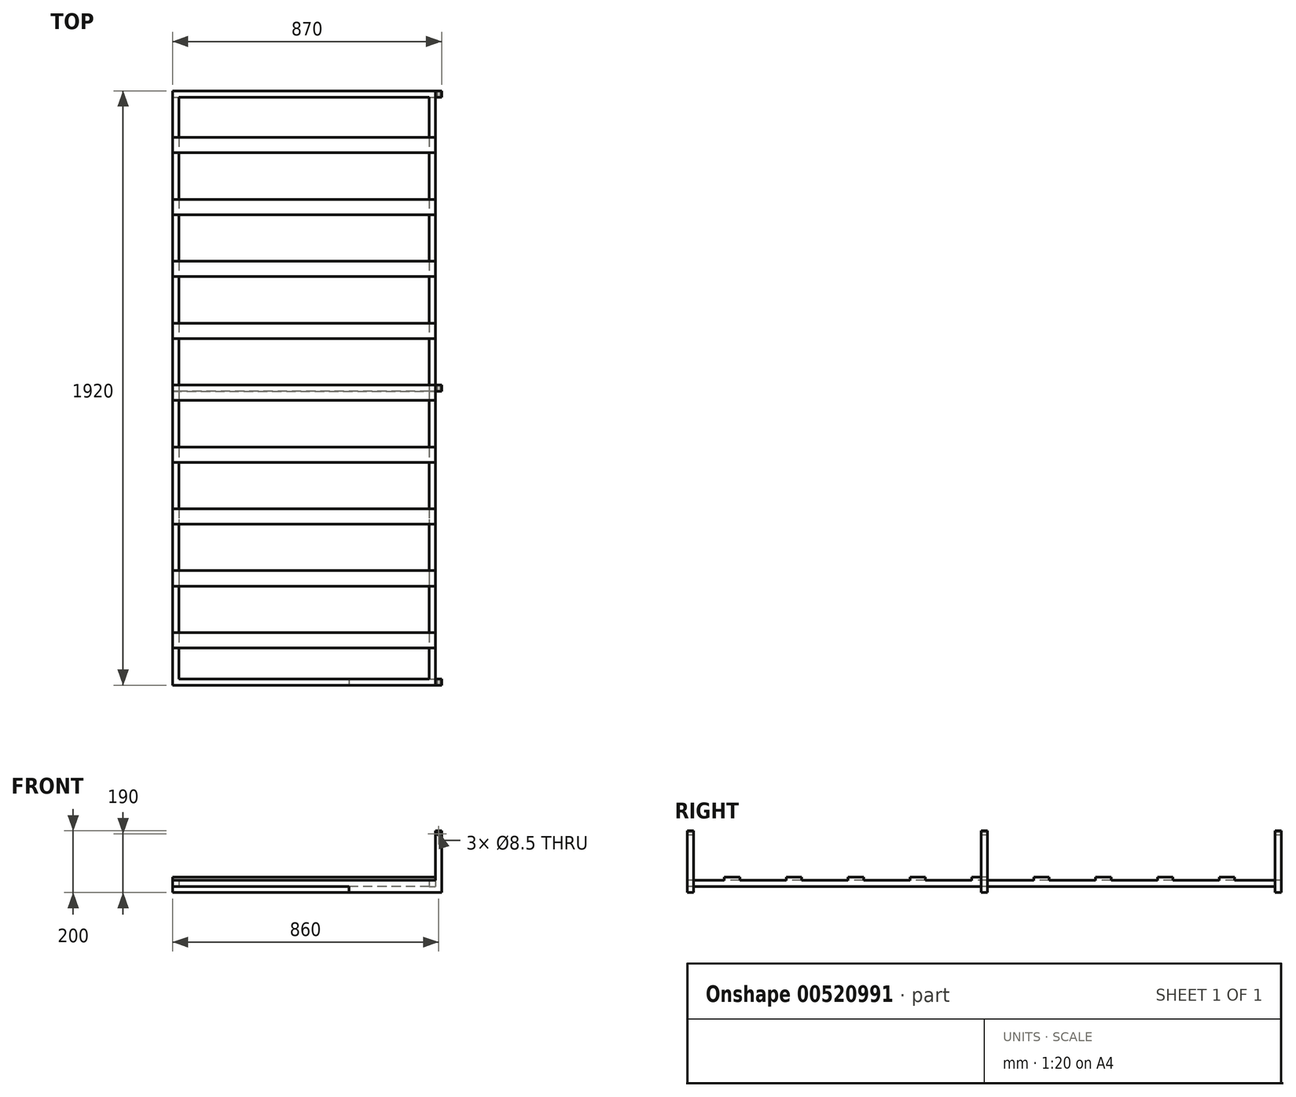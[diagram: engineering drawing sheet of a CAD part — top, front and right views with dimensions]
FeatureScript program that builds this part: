
annotation { "Feature Type Name" : "Feature", "Feature Type Description" : "" }
export const myFeature = defineFeature(function(context is Context, id is Id, definition is map)
    precondition{}
    {
        {
            var Q0;
            Q0=qCreatedBy(makeId("Top.planeOp"),FACE);
            var sketch = newSketch(context, id + "F0", { "sketchPlane" : qUnion([Q0])});
            skLineSegment(sketch, "E0.bottom", {"start": v(-425, 960) * mm, "end": v(425, 960) * mm});
            skLineSegment(sketch, "E0.top", {"start": v(-425, -960) * mm, "end": v(425, -960) * mm});
            skLineSegment(sketch, "E0.left", {"start": v(-425, 960) * mm, "end": v(-425, -960) * mm});
            skLineSegment(sketch, "E0.right", {"start": v(425, 960) * mm, "end": v(425, -960) * mm});
            skPoint(sketch, "E0.middle", {"position": v(0, 0) * mm});
            skLineSegment(sketch, "E1.0", {"start": v(405, 940) * mm, "end": v(405, -940) * mm});
            skLineSegment(sketch, "E1.1", {"start": v(-405, 940) * mm, "end": v(405, 940) * mm});
            skLineSegment(sketch, "E1.2", {"start": v(-405, 940) * mm, "end": v(-405, -940) * mm});
            skLineSegment(sketch, "E1.3", {"start": v(-405, -940) * mm, "end": v(405, -940) * mm});
            skSolve(sketch);
        }
        {
            var Q0;
            Q0 = qSketchRegion(id + "F0", true);
            extrude(context, id + "F1", {"entities" : qUnion([Q0]), "depth" : 20 * mm, "offsetDistance" : 25 * mm});
        }
        {
            var Q0;
            Q0=makeQuery(id+"F1.opExtrude","CAP_FACE",FACE,{"disambiguationData":[OSD([sQuery(id+"F0.wireOp",EDGE,"E0.bottom"),sQuery(id+"F0.wireOp",EDGE,"E0.top"),sQuery(id+"F0.wireOp",EDGE,"E0.left"),sQuery(id+"F0.wireOp",EDGE,"E0.right"),sQuery(id+"F0.wireOp",EDGE,"E1.0"),sQuery(id+"F0.wireOp",EDGE,"E1.1"),sQuery(id+"F0.wireOp",EDGE,"E1.2"),sQuery(id+"F0.wireOp",EDGE,"E1.3")])],"isStart":false});
            var sketch = newSketch(context, id + "F2", { "sketchPlane" : qUnion([Q0])});
            skLineSegment(sketch, "E2.bottom", {"start": v(-425, 810) * mm, "end": v(425, 810) * mm});
            skLineSegment(sketch, "E2.top", {"start": v(-425, 760) * mm, "end": v(425, 760) * mm});
            skLineSegment(sketch, "E2.left", {"start": v(-425, 810) * mm, "end": v(-425, 760) * mm});
            skLineSegment(sketch, "E2.right", {"start": v(425, 810) * mm, "end": v(425, 760) * mm});
            skLineSegment(sketch, "E3.0.1.0", {"start": v(-425, 560) * mm, "end": v(425, 560) * mm});
            skLineSegment(sketch, "E3.0.1.1", {"start": v(-425, 610) * mm, "end": v(425, 610) * mm});
            skLineSegment(sketch, "E3.0.1.2", {"start": v(-425, 610) * mm, "end": v(-425, 560) * mm});
            skLineSegment(sketch, "E3.0.1.3", {"start": v(425, 610) * mm, "end": v(425, 560) * mm});
            skLineSegment(sketch, "E3.0.2.0", {"start": v(-425, 360) * mm, "end": v(425, 360) * mm});
            skLineSegment(sketch, "E3.0.2.1", {"start": v(-425, 410) * mm, "end": v(425, 410) * mm});
            skLineSegment(sketch, "E3.0.2.2", {"start": v(-425, 410) * mm, "end": v(-425, 360) * mm});
            skLineSegment(sketch, "E3.0.2.3", {"start": v(425, 410) * mm, "end": v(425, 360) * mm});
            skLineSegment(sketch, "E3.0.3.0", {"start": v(-425, 160) * mm, "end": v(425, 160) * mm});
            skLineSegment(sketch, "E3.0.3.1", {"start": v(-425, 210) * mm, "end": v(425, 210) * mm});
            skLineSegment(sketch, "E3.0.3.2", {"start": v(-425, 210) * mm, "end": v(-425, 160) * mm});
            skLineSegment(sketch, "E3.0.3.3", {"start": v(425, 210) * mm, "end": v(425, 160) * mm});
            skLineSegment(sketch, "E3.0.4.0", {"start": v(-425, -40) * mm, "end": v(425, -40) * mm});
            skLineSegment(sketch, "E3.0.4.1", {"start": v(-425, 10) * mm, "end": v(425, 10) * mm});
            skLineSegment(sketch, "E3.0.4.2", {"start": v(-425, 10) * mm, "end": v(-425, -40) * mm});
            skLineSegment(sketch, "E3.0.4.3", {"start": v(425, 10) * mm, "end": v(425, -40) * mm});
            skLineSegment(sketch, "E3.0.5.0", {"start": v(-425, -240) * mm, "end": v(425, -240) * mm});
            skLineSegment(sketch, "E3.0.5.1", {"start": v(-425, -190) * mm, "end": v(425, -190) * mm});
            skLineSegment(sketch, "E3.0.5.2", {"start": v(-425, -190) * mm, "end": v(-425, -240) * mm});
            skLineSegment(sketch, "E3.0.5.3", {"start": v(425, -190) * mm, "end": v(425, -240) * mm});
            skLineSegment(sketch, "E3.0.6.0", {"start": v(-425, -440) * mm, "end": v(425, -440) * mm});
            skLineSegment(sketch, "E3.0.6.1", {"start": v(-425, -390) * mm, "end": v(425, -390) * mm});
            skLineSegment(sketch, "E3.0.6.2", {"start": v(-425, -390) * mm, "end": v(-425, -440) * mm});
            skLineSegment(sketch, "E3.0.6.3", {"start": v(425, -390) * mm, "end": v(425, -440) * mm});
            skLineSegment(sketch, "E3.0.7.0", {"start": v(-425, -640) * mm, "end": v(425, -640) * mm});
            skLineSegment(sketch, "E3.0.7.1", {"start": v(-425, -590) * mm, "end": v(425, -590) * mm});
            skLineSegment(sketch, "E3.0.7.2", {"start": v(-425, -590) * mm, "end": v(-425, -640) * mm});
            skLineSegment(sketch, "E3.0.7.3", {"start": v(425, -590) * mm, "end": v(425, -640) * mm});
            skLineSegment(sketch, "E3.0.8.0", {"start": v(-425, -840) * mm, "end": v(425, -840) * mm});
            skLineSegment(sketch, "E3.0.8.1", {"start": v(-425, -790) * mm, "end": v(425, -790) * mm});
            skLineSegment(sketch, "E3.0.8.2", {"start": v(-425, -790) * mm, "end": v(-425, -840) * mm});
            skLineSegment(sketch, "E3.0.8.3", {"start": v(425, -790) * mm, "end": v(425, -840) * mm});
            skLineSegment(sketch, "E3.direction1", {"start": v(-425, 760) * mm, "end": v(-400, 760) * mm, "construction": true});
            skLineSegment(sketch, "E3.direction2", {"start": v(-425, 760) * mm, "end": v(-425, 560) * mm, "construction": true});
            skSolve(sketch);
        }
        {
            var Q0;
            Q0 = qSketchRegion(id + "F2", true);
            extrude(context, id + "F3", {"entities" : qUnion([Q0]), "operationType" : NewBodyOperationType.ADD, "depth" : 10 * mm, "offsetDistance" : 25 * mm});
        }
        {
            var Q0;
            Q0=qCreatedBy(makeId("Front.planeOp"),FACE);
            cPlane(context, id + "F4", {"entities" : qUnion([Q0]), "cplaneType" : CPlaneType.OFFSET, "offset" : 800 * mm, "width" : 150 * mm, "height" : 150 * mm});
        }
        {
            var Q0;
            Q0=makeQuery(id+"F1.opExtrude","SWEPT_FACE",FACE,{"disambiguationData":[OSD([sQuery(id+"F0.wireOp",EDGE,"E0.top")])]});
            var sketch = newSketch(context, id + "F5", { "sketchPlane" : qUnion([Q0])});
            skLineSegment(sketch, "E4", {"start": v(425, 180) * mm, "end": v(425, 0) * mm});
            skLineSegment(sketch, "E5", {"start": v(425, 0) * mm, "end": v(145, 0) * mm});
            skLineSegment(sketch, "E6", {"start": v(145, 0) * mm, "end": v(145, -20) * mm});
            skLineSegment(sketch, "E7", {"start": v(145, -20) * mm, "end": v(445, -20) * mm});
            skLineSegment(sketch, "E8", {"start": v(445, -20) * mm, "end": v(445, 180) * mm});
            skLineSegment(sketch, "E9", {"start": v(445, 180) * mm, "end": v(425, 180) * mm});
            skSolve(sketch);
        }
        {
            var Q0;
            Q0 = qSketchRegion(id + "F5", true);
            extrude(context, id + "F6", {"entities" : qUnion([Q0]), "operationType" : NewBodyOperationType.ADD, "oppositeDirection" : true, "depth" : 20 * mm, "offsetDistance" : 25 * mm});
        }
        {
            var Q0;
            Q0=qCreatedBy(makeId("Front.planeOp"),FACE);
            var sketch = newSketch(context, id + "F7", { "sketchPlane" : qUnion([Q0])});
            skLineSegment(sketch, "E10", {"start": v(-425, 0) * mm, "end": v(-425, -20) * mm});
            skLineSegment(sketch, "E11", {"start": v(-425, -20) * mm, "end": v(445, -20) * mm});
            skLineSegment(sketch, "E12", {"start": v(445, -20) * mm, "end": v(445, 180) * mm});
            skLineSegment(sketch, "E13", {"start": v(445, 180) * mm, "end": v(425, 180) * mm});
            skLineSegment(sketch, "E14", {"start": v(425, 180) * mm, "end": v(425, 0) * mm});
            skLineSegment(sketch, "E15", {"start": v(425, 0) * mm, "end": v(-425, 0) * mm});
            skSolve(sketch);
        }
        {
            var Q0;
            Q0 = qSketchRegion(id + "F7", true);
            extrude(context, id + "F8", {"entities" : qUnion([Q0]), "operationType" : NewBodyOperationType.ADD, "depth" : 10 * mm, "offsetDistance" : 25 * mm, "hasSecondDirection" : true, "secondDirectionOppositeDirection" : true, "secondDirectionDepth" : 10 * mm});
        }
        {
            var Q0;
            Q0=makeQuery(id+"F1.opExtrude","SWEPT_FACE",FACE,{"disambiguationData":[OSD([sQuery(id+"F0.wireOp",EDGE,"E0.bottom")])]});
            var sketch = newSketch(context, id + "F9", { "sketchPlane" : qUnion([Q0])});
            skLineSegment(sketch, "E16", {"start": v(-425, 0) * mm, "end": v(-425, 180) * mm});
            skLineSegment(sketch, "E17", {"start": v(-425, 180) * mm, "end": v(-445, 180) * mm});
            skLineSegment(sketch, "E18", {"start": v(-445, 180) * mm, "end": v(-445, -20) * mm});
            skLineSegment(sketch, "E19", {"start": v(-445, -20) * mm, "end": v(425, -20) * mm});
            skLineSegment(sketch, "E20", {"start": v(425, -20) * mm, "end": v(425, 0) * mm});
            skLineSegment(sketch, "E21", {"start": v(425, 0) * mm, "end": v(-425, 0) * mm});
            skSolve(sketch);
        }
        {
            var Q0;
            Q0 = qSketchRegion(id + "F9", true);
            extrude(context, id + "F10", {"entities" : qUnion([Q0]), "operationType" : NewBodyOperationType.ADD, "oppositeDirection" : true, "depth" : 20 * mm, "offsetDistance" : 25 * mm});
        }
        {
            var Q0;
            Q0=qCreatedBy(makeId("Front.planeOp"),FACE);
            var sketch = newSketch(context, id + "F11", { "sketchPlane" : qUnion([Q0])});
            skCircle(sketch, "E22", {"center": v(435, 170) * mm, "radius": 4.25 * mm});
            skSolve(sketch);
        }
        {
            var Q0;
            Q0 = qSketchRegion(id + "F11", true);
            extrude(context, id + "F12", {"entities" : qUnion([Q0]), "operationType" : NewBodyOperationType.REMOVE, "endBound" : BoundingType.THROUGH_ALL, "oppositeDirection" : true, "depth" : 25 * mm, "offsetDistance" : 25 * mm, "hasSecondDirection" : true, "secondDirectionBound" : SecondDirectionBoundingType.THROUGH_ALL, "secondDirectionOppositeDirection" : false, "secondDirectionDepth" : 25 * mm});
        }
    });
